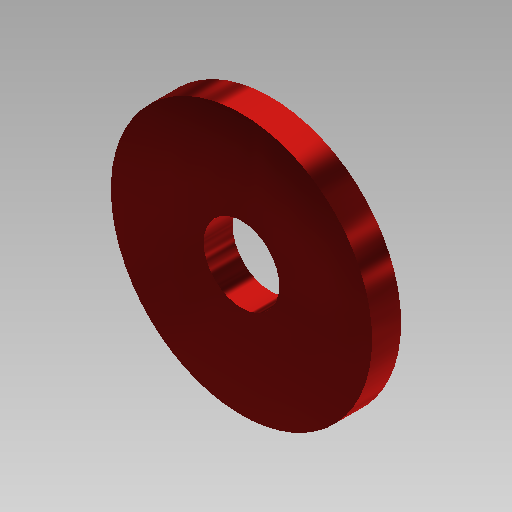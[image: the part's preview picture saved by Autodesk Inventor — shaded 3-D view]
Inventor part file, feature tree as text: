
AUTODESK INVENTOR PART (.ipt)
format: ipt  version: 2018.1 (Build 221171000, 171)  size: 101,888 bytes
history: native  units: in
note: dims shown in document units (in); Inventor stores cm internally (conversion verified against a paired STEP export)
features: extrude x1, sketch x1
ambient origin geometry x8: Origin, YZ Plane, XZ Plane, XY Plane, X Axis, Y Axis, Z Axis, Center Point
bodies: Solid1 (feature_tree)
feature tree (2):
  extrude  "Extrusion1"  Depth=0.0787in
  sketch  "Sketch1"  dims[d0=0.7087in d1=0.2047in d2=0.0787in d3=0.0in]
